# Revit family: Legrand_Gestion_eclairage_Detecteur_Presence_Mur_SCS
name_source: partatom
category: Dispositifs d'éclairage
units: mm (PartAtom-declared; Revit-internal decimal feet)

## family parameters
Conserver l'orientation des annotations = Oui
Cote de connecteur circulaire = Utiliser le diamètre
Couper avec des vides une fois chargée = Non
Hôte = Face
Partagée = Non
Point de calcul de pièce = Non
Type d'élément = Normal

## types (1)
- Saillie SCS - PIR - IP55
    Adapté pour transmission sans fil = Non
    Angle de détection horizontal (MAX) (°) = 180
    Angle de détection horizontal (MIN) (°) = 180
    Capacité de coupure max. (W) = 0
    Collecteur de terre = Non
    Condition Générale d'Utilisation = https://export.legrand.com
    Cosses d'artère secondaire = Non
    Couleur = Blanc
    Coupure forcée = Non
    Courant de démarrage max. (A) = 0
    Description = Détecteur de mouvement parkings extérieurs et caves - IP55 - IR- saillie mur
    Diamètre de détection sur le plancher (m) = 3.5
    Durée d'enclenchement max. (mn) = 1000
    Durée d'enclenchement min. (s) = 30
    Elévation par défaut = 2500 mm  [stored 8.2021 ft]
    Entrée secondaire = Non
    Exécution - Modèle = détecteur de mouvement
    Fabricant = Legrand
    Fonction variateur intégré = Non
    Fréquence (MAX) (Hz) = 0
    Fréquence (MIN) (Hz) = 0
    Gestion CVC = Non
    Gestion alarme = Non
    Hauteur de montage maximale (m) = 2.5
    Liaison neutre = Non
    Mode de montage = apparent
    Modèle = 048834
    Numéro RAL = 9003
    Portée max. frontale (m) = 15
    Portée max. latérale (m) = 3.5
    Réglage de lumière constante = Non
    Sensibilité lumineuse (MAX) (lx) = 0
    Sensibilité lumineuse (MIN) (lx) = 0
    Sensibilité lumineuse réglable = Oui
    Sensibilité réglable = Non
    Température (MAX) (°C) = 0
    Température (MIN) (°C) = 0
    Tension nominale (V) = 0
    Télécommandable = Non
    URL = http://www.legrandoc.com

note: [stored X ft] marks values corroborated as IEEE doubles in the binary element streams (Revit-internal decimal feet)
